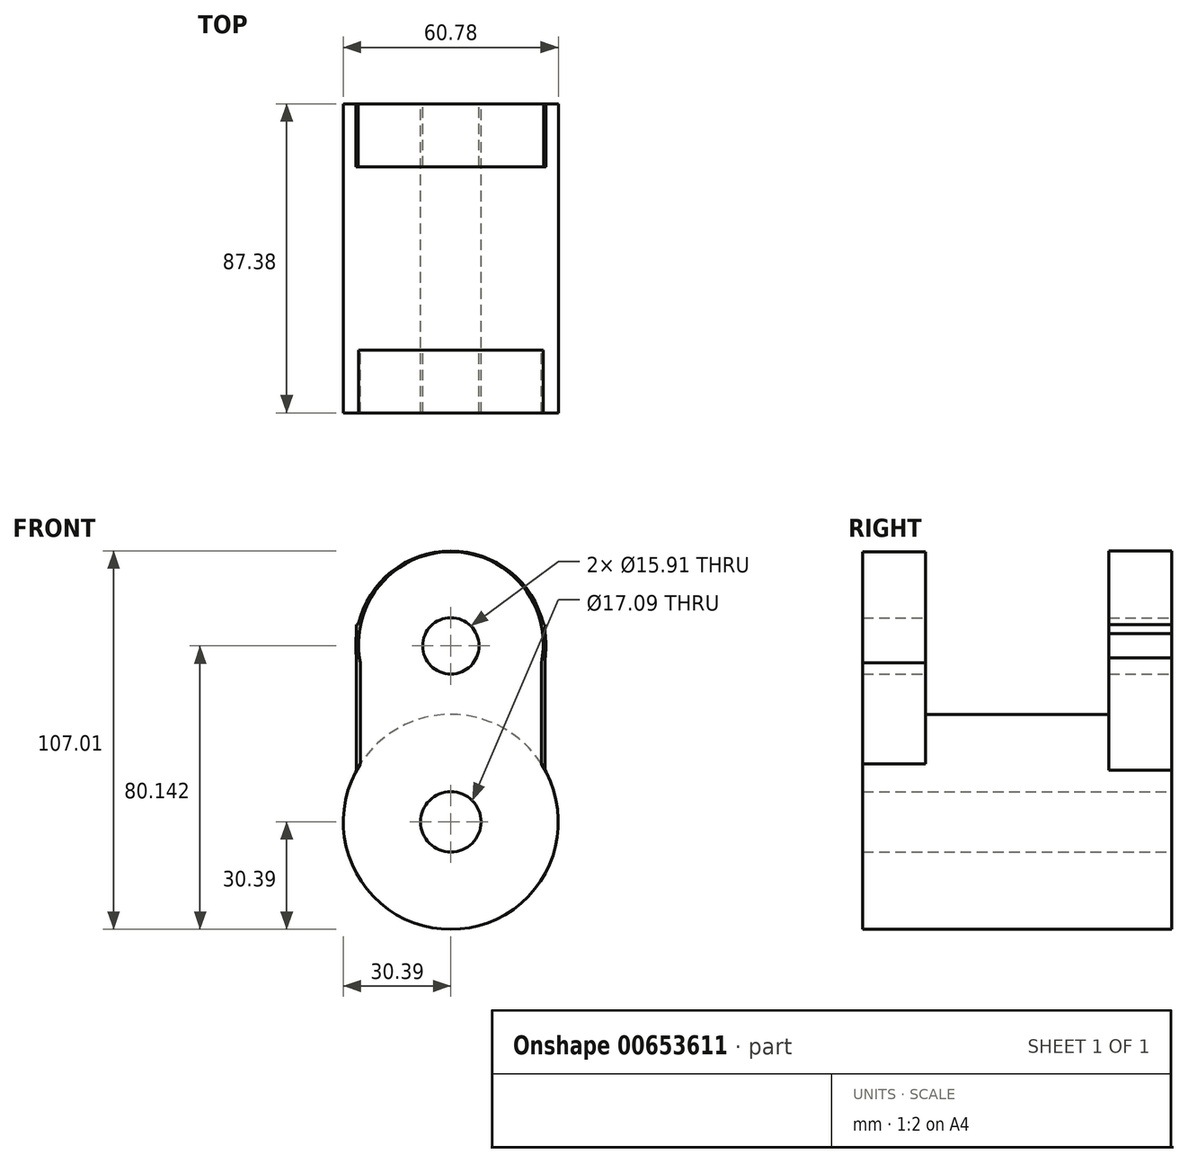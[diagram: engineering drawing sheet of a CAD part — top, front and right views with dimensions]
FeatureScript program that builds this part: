
annotation { "Feature Type Name" : "Feature", "Feature Type Description" : "" }
export const myFeature = defineFeature(function(context is Context, id is Id, definition is map)
    precondition{}
    {
        {
            var Q0;
            Q0=qCreatedBy(makeId("Front.planeOp"),FACE);
            var sketch = newSketch(context, id + "F0", { "sketchPlane" : qUnion([Q0])});
            skCircle(sketch, "E0", {"center": v(0, 0) * mm, "radius": 30.4 * mm});
            skSolve(sketch);
        }
        {
            var Q0;
            Q0=makeQuery(id+"F0.imprint","IMPRINT",FACE,{"disambiguationData":[TD([[makeQuery(id+"F0.imprint","IMPRINT",EDGE,{"derivedFrom":sQuery(id+"F0.wireOp",EDGE,"E0")}),1.0]])]});
            extrude(context, id + "F1", {"entities" : qUnion([Q0]), "endBound" : BoundingType.SYMMETRIC, "depth" : 87.38 * mm, "offsetDistance" : 25.4 * mm});
        }
        {
            var Q0;
            Q0=makeQuery(id+"F1.opExtrude","CAP_FACE",FACE,{"disambiguationData":[OSD([sQuery(id+"F0.wireOp",EDGE,"E0")])],"isStart":false});
            var sketch = newSketch(context, id + "F2", { "sketchPlane" : qUnion([Q0])});
            skLineSegment(sketch, "E1", {"start": v(-25.59, -16.4) * mm, "end": v(-25.59, 54.98) * mm});
            skLineSegment(sketch, "E2", {"start": v(-25.59, 54.98) * mm, "end": v(25.59, 54.98) * mm});
            skLineSegment(sketch, "E3", {"start": v(25.59, 54.98) * mm, "end": v(25.59, -16.4) * mm});
            skLineSegment(sketch, "E4", {"start": v(25.59, -16.4) * mm, "end": v(-25.59, -16.4) * mm});
            skSolve(sketch);
        }
        {
            var Q0;
            {var subQ0=sQuery(id+"F2.wireOp",EDGE,"E2");Q0=makeQuery(id+"F2.imprint","IMPRINT",FACE,{"disambiguationData":[TD([[makeQuery(id+"F2.imprint","IMPRINT",EDGE,{"derivedFrom":subQ0}),-1.0]])]});}
            var Q1;
            {var subQ0=sQuery(id+"F2.wireOp",EDGE,"E4");Q1=makeQuery(id+"F2.imprint","IMPRINT",FACE,{"disambiguationData":[TD([[makeQuery(id+"F2.imprint","IMPRINT",EDGE,{"derivedFrom":subQ0}),-1.0]])]});}
            extrude(context, id + "F3", {"entities" : qUnion([Q0, Q1]), "operationType" : NewBodyOperationType.ADD, "oppositeDirection" : true, "depth" : 17.78 * mm, "offsetDistance" : 25.4 * mm});
        }
        {
            var Q0;
            Q0=makeQuery(id+"F1.opExtrude","CAP_FACE",FACE,{"disambiguationData":[OSD([sQuery(id+"F0.wireOp",EDGE,"E0")])],"isStart":true});
            var sketch = newSketch(context, id + "F4", { "sketchPlane" : qUnion([Q0])});
            skLineSegment(sketch, "E5", {"start": v(-26.65, -14.61) * mm, "end": v(-26.65, 55.73) * mm});
            skLineSegment(sketch, "E6", {"start": v(-26.65, 55.73) * mm, "end": v(26.65, 55.73) * mm});
            skLineSegment(sketch, "E7", {"start": v(26.65, 55.73) * mm, "end": v(26.65, -14.61) * mm});
            skLineSegment(sketch, "E8", {"start": v(26.65, -14.61) * mm, "end": v(-26.65, -14.61) * mm});
            skSolve(sketch);
        }
        {
            var Q0;
            {var subQ0=sQuery(id+"F4.wireOp",EDGE,"E6");Q0=makeQuery(id+"F4.imprint","IMPRINT",FACE,{"disambiguationData":[TD([[makeQuery(id+"F4.imprint","IMPRINT",EDGE,{"derivedFrom":subQ0}),-1.0]])]});}
            var Q1;
            {var subQ0=sQuery(id+"F4.wireOp",EDGE,"E8");Q1=makeQuery(id+"F4.imprint","IMPRINT",FACE,{"disambiguationData":[TD([[makeQuery(id+"F4.imprint","IMPRINT",EDGE,{"derivedFrom":subQ0}),-1.0]])]});}
            extrude(context, id + "F5", {"entities" : qUnion([Q0, Q1]), "operationType" : NewBodyOperationType.ADD, "oppositeDirection" : true, "depth" : 17.78 * mm, "offsetDistance" : 25.4 * mm});
        }
        {
            var Q0;
            Q0=makeQuery(id+"F5.boolean.opBoolean","MERGE",FACE,{"derivedFrom":[makeQuery(id+"F1.opExtrude","CAP_FACE",FACE,{"disambiguationData":[OSD([sQuery(id+"F0.wireOp",EDGE,"E0")])],"isStart":true}),makeQuery(id+"F5.opExtrude","CAP_FACE",FACE,{"disambiguationData":[OSD([sQuery(id+"F4.wireOp",EDGE,"E5"),sQuery(id+"F4.wireOp",EDGE,"E6"),sQuery(id+"F4.wireOp",EDGE,"E7"),sQuery(id+"F4.wireOp",EDGE,"E8")])],"isStart":true})]});
            var sketch = newSketch(context, id + "F6", { "sketchPlane" : qUnion([Q0])});
            skCircle(sketch, "E9", {"center": v(0, 0) * mm, "radius": 8.54 * mm});
            skSolve(sketch);
        }
        {
            var Q0;
            Q0=makeQuery(id+"F6.imprint","IMPRINT",FACE,{"disambiguationData":[TD([[makeQuery(id+"F6.imprint","IMPRINT",EDGE,{"derivedFrom":sQuery(id+"F6.wireOp",EDGE,"E9")}),1.0]])]});
            extrude(context, id + "F7", {"entities" : qUnion([Q0]), "operationType" : NewBodyOperationType.REMOVE, "oppositeDirection" : true, "depth" : 104.14 * mm, "offsetDistance" : 25.4 * mm});
        }
        {
            var Q0;
            Q0=makeQuery(id+"F3.boolean.opBoolean","MERGE",FACE,{"derivedFrom":[makeQuery(id+"F1.opExtrude","CAP_FACE",FACE,{"disambiguationData":[OSD([sQuery(id+"F0.wireOp",EDGE,"E0")])],"isStart":false}),makeQuery(id+"F3.opExtrude","CAP_FACE",FACE,{"disambiguationData":[OSD([sQuery(id+"F2.wireOp",EDGE,"E1"),sQuery(id+"F2.wireOp",EDGE,"E2"),sQuery(id+"F2.wireOp",EDGE,"E3"),sQuery(id+"F2.wireOp",EDGE,"E4")])],"isStart":true})]});
            var sketch = newSketch(context, id + "F8", { "sketchPlane" : qUnion([Q0])});
            skCircle(sketch, "E10", {"center": v(0, 50.24) * mm, "radius": 26.12 * mm});
            skSolve(sketch);
        }
        {
            var Q0;
            Q0 = qSketchRegion(id + "F8", true);
            extrude(context, id + "F9", {"entities" : qUnion([Q0]), "operationType" : NewBodyOperationType.ADD, "oppositeDirection" : true, "depth" : 17.78 * mm, "offsetDistance" : 25.4 * mm});
        }
        {
            var Q0;
            Q0=makeQuery(id+"F5.boolean.opBoolean","MERGE",FACE,{"derivedFrom":[makeQuery(id+"F1.opExtrude","CAP_FACE",FACE,{"disambiguationData":[OSD([sQuery(id+"F0.wireOp",EDGE,"E0")])],"isStart":true}),makeQuery(id+"F5.opExtrude","CAP_FACE",FACE,{"disambiguationData":[OSD([sQuery(id+"F4.wireOp",EDGE,"E5"),sQuery(id+"F4.wireOp",EDGE,"E6"),sQuery(id+"F4.wireOp",EDGE,"E7"),sQuery(id+"F4.wireOp",EDGE,"E8")])],"isStart":true})]});
            var sketch = newSketch(context, id + "F10", { "sketchPlane" : qUnion([Q0])});
            skCircle(sketch, "E11", {"center": v(0, 49.75) * mm, "radius": 26.86 * mm});
            skSolve(sketch);
        }
        {
            var Q0;
            Q0 = qSketchRegion(id + "F10", true);
            extrude(context, id + "F11", {"entities" : qUnion([Q0]), "operationType" : NewBodyOperationType.ADD, "oppositeDirection" : true, "depth" : 17.78 * mm, "offsetDistance" : 25.4 * mm});
        }
        {
            var Q0;
            Q0=makeQuery(id+"F11.boolean.opBoolean","MERGE",FACE,{"derivedFrom":[makeQuery(id+"F5.boolean.opBoolean","MERGE",FACE,{"derivedFrom":[makeQuery(id+"F1.opExtrude","CAP_FACE",FACE,{"disambiguationData":[OSD([sQuery(id+"F0.wireOp",EDGE,"E0")])],"isStart":true}),makeQuery(id+"F5.opExtrude","CAP_FACE",FACE,{"disambiguationData":[OSD([sQuery(id+"F4.wireOp",EDGE,"E5"),sQuery(id+"F4.wireOp",EDGE,"E6"),sQuery(id+"F4.wireOp",EDGE,"E7"),sQuery(id+"F4.wireOp",EDGE,"E8")])],"isStart":true})]}),makeQuery(id+"F11.opExtrude","CAP_FACE",FACE,{"disambiguationData":[OSD([sQuery(id+"F10.wireOp",EDGE,"E11")])],"isStart":true})]});
            var sketch = newSketch(context, id + "F12", { "sketchPlane" : qUnion([Q0])});
            skCircle(sketch, "E12", {"center": v(0, 49.75) * mm, "radius": 7.95 * mm});
            skSolve(sketch);
        }
        {
            var Q0;
            Q0 = qSketchRegion(id + "F12", true);
            extrude(context, id + "F13", {"entities" : qUnion([Q0]), "operationType" : NewBodyOperationType.REMOVE, "oppositeDirection" : true, "depth" : 97.8 * mm, "offsetDistance" : 25.4 * mm});
        }
    });
